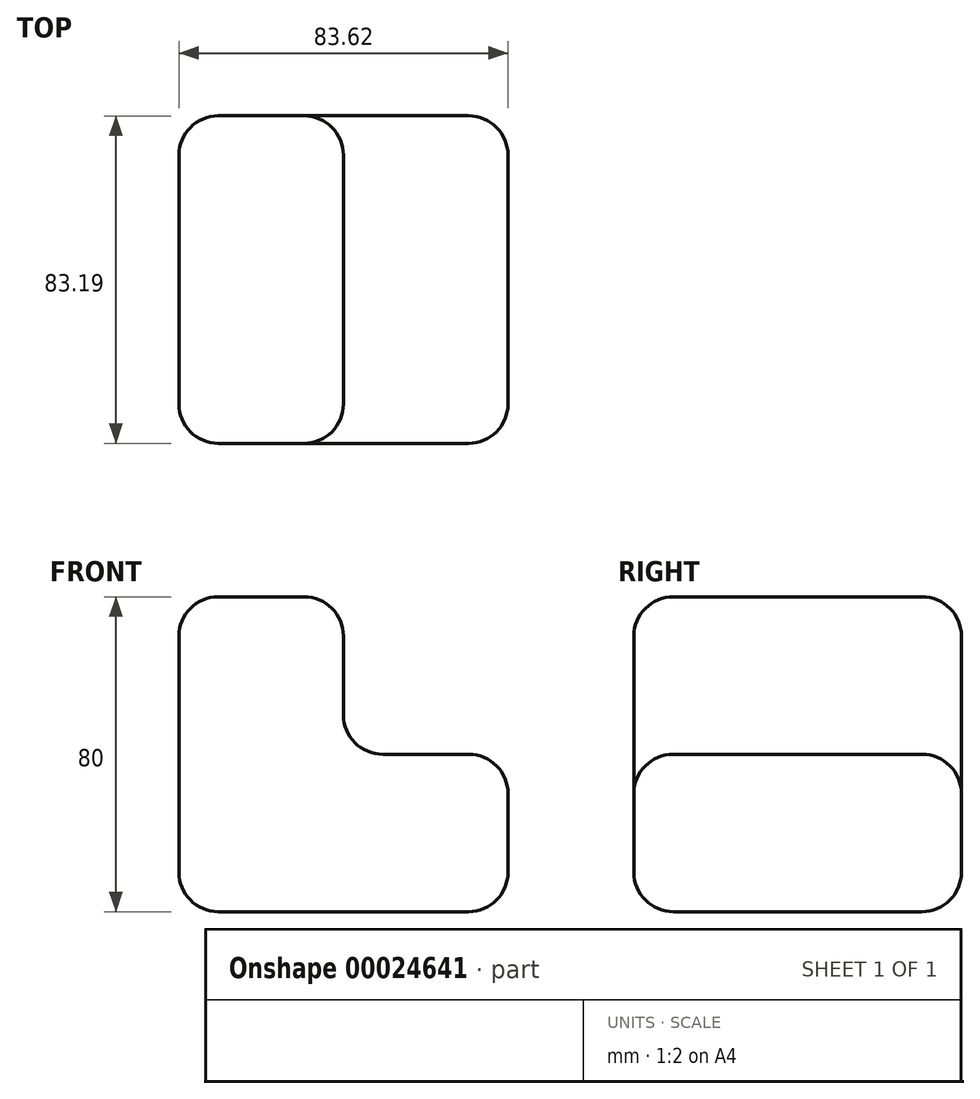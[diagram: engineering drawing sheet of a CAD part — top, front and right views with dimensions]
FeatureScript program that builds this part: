
annotation { "Feature Type Name" : "Feature", "Feature Type Description" : "" }
export const myFeature = defineFeature(function(context is Context, id is Id, definition is map)
    precondition{}
    {
        {
            var Q0;
            Q0=qCreatedBy(makeId("Top.planeOp"),FACE);
            var sketch = newSketch(context, id + "F0", { "sketchPlane" : qUnion([Q0])});
            skLineSegment(sketch, "E0.bottom", {"start": v(-59.13, -45.93) * mm, "end": v(24.5, -45.93) * mm});
            skLineSegment(sketch, "E0.top", {"start": v(-59.13, 37.26) * mm, "end": v(24.5, 37.26) * mm});
            skLineSegment(sketch, "E0.left", {"start": v(-59.13, -45.93) * mm, "end": v(-59.13, 37.26) * mm});
            skLineSegment(sketch, "E0.right", {"start": v(24.5, -45.93) * mm, "end": v(24.5, 37.26) * mm});
            skSolve(sketch);
        }
        {
            var Q0;
            Q0=makeQuery(id+"F0.imprint","IMPRINT",FACE,{"disambiguationData":[TD([[makeQuery(id+"F0.imprint","IMPRINT",EDGE,{"derivedFrom":sQuery(id+"F0.wireOp",EDGE,"E0.bottom")}),1.0]])]});
            extrude(context, id + "F1", {"entities" : qUnion([Q0]), "depth" : 40 * mm});
        }
        {
            var Q0;
            Q0=makeQuery(id+"F1.opExtrude","CAP_FACE",FACE,{"disambiguationData":[OSD([sQuery(id+"F0.wireOp",EDGE,"E0.bottom"),sQuery(id+"F0.wireOp",EDGE,"E0.top"),sQuery(id+"F0.wireOp",EDGE,"E0.left"),sQuery(id+"F0.wireOp",EDGE,"E0.right")])],"isStart":false});
            var sketch = newSketch(context, id + "F2", { "sketchPlane" : qUnion([Q0])});
            skLineSegment(sketch, "E1", {"start": v(-17.32, 37.26) * mm, "end": v(-17.32, -45.93) * mm});
            skSolve(sketch);
        }
        {
            var Q0;
            {var subQ1=sQuery(id+"F2.wireOp",EDGE,"E1");Q0=makeQuery(id+"F2.imprint","IMPRINT",FACE,{"disambiguationData":[TD([[makeQuery(id+"F2.imprint","IMPRINT",EDGE,{"derivedFrom":subQ1}),-1.0]])]});}
            extrude(context, id + "F3", {"entities" : qUnion([Q0]), "operationType" : NewBodyOperationType.ADD, "depth" : 40 * mm});
        }
        {
            var Q0;
            Q0=makeQuery(id+"F3.opExtrude","CAP_EDGE",EDGE,{"disambiguationData":[OSD([sQuery(id+"F0.wireOp",EDGE,"E0.bottom")])],"isStart":false});
            var Q1;
            Q1=makeQuery(id+"F3.opExtrude","CAP_EDGE",EDGE,{"disambiguationData":[OSD([sQuery(id+"F2.wireOp",EDGE,"E1")])],"isStart":false});
            var Q2;
            {var subQ0=sQuery(id+"F0.wireOp",EDGE,"E0.bottom");Q2=makeQuery(id+"F3.boolean.opBoolean","MERGE",FACE,{"derivedFrom":[makeQuery(id+"F1.opExtrude","SWEPT_FACE",FACE,{"disambiguationData":[OSD([subQ0])]}),makeQuery(id+"F3.opExtrude","SWEPT_FACE",FACE,{"disambiguationData":[OSD([subQ0])]})]});}
            var Q3;
            Q3=makeQuery(id+"F1.opExtrude","SWEPT_FACE",FACE,{"disambiguationData":[OSD([sQuery(id+"F0.wireOp",EDGE,"E0.right")])]});
            var Q4;
            Q4=makeQuery(id+"F3.opExtrude","SWEPT_FACE",FACE,{"disambiguationData":[OSD([sQuery(id+"F2.wireOp",EDGE,"E1")])]});
            var Q5;
            Q5=makeQuery(id+"F1.opExtrude","CAP_FACE",FACE,{"disambiguationData":[OSD([sQuery(id+"F0.wireOp",EDGE,"E0.bottom"),sQuery(id+"F0.wireOp",EDGE,"E0.top"),sQuery(id+"F0.wireOp",EDGE,"E0.left"),sQuery(id+"F0.wireOp",EDGE,"E0.right")])],"isStart":false});
            var Q6;
            Q6=makeQuery(id+"F3.opExtrude","CAP_FACE",FACE,{"disambiguationData":[OSD([sQuery(id+"F0.wireOp",EDGE,"E0.bottom"),sQuery(id+"F0.wireOp",EDGE,"E0.top"),sQuery(id+"F0.wireOp",EDGE,"E0.left"),sQuery(id+"F2.wireOp",EDGE,"E1")])],"isStart":false});
            var Q7;
            {var subQ0=sQuery(id+"F0.wireOp",EDGE,"E0.top");Q7=makeQuery(id+"F3.boolean.opBoolean","MERGE",FACE,{"derivedFrom":[makeQuery(id+"F1.opExtrude","SWEPT_FACE",FACE,{"disambiguationData":[OSD([subQ0])]}),makeQuery(id+"F3.opExtrude","SWEPT_FACE",FACE,{"disambiguationData":[OSD([subQ0])]})]});}
            var Q8;
            Q8=makeQuery(id+"F1.opExtrude","CAP_FACE",FACE,{"disambiguationData":[OSD([sQuery(id+"F0.wireOp",EDGE,"E0.bottom"),sQuery(id+"F0.wireOp",EDGE,"E0.top"),sQuery(id+"F0.wireOp",EDGE,"E0.left"),sQuery(id+"F0.wireOp",EDGE,"E0.right")])],"isStart":true});
            var Q9;
            {var subQ0=sQuery(id+"F0.wireOp",EDGE,"E0.left");Q9=makeQuery(id+"F3.boolean.opBoolean","MERGE",FACE,{"derivedFrom":[makeQuery(id+"F1.opExtrude","SWEPT_FACE",FACE,{"disambiguationData":[OSD([subQ0])]}),makeQuery(id+"F3.opExtrude","SWEPT_FACE",FACE,{"disambiguationData":[OSD([subQ0])]})]});}
            fillet(context, id + "F4", {"entities" : qUnion([Q0, Q1, Q2, Q3, Q4, Q5, Q6, Q7, Q8, Q9]), "radius" : 10 * mm, "tangentPropagation" : true, "allowEdgeOverflow" : false});
        }
    });
